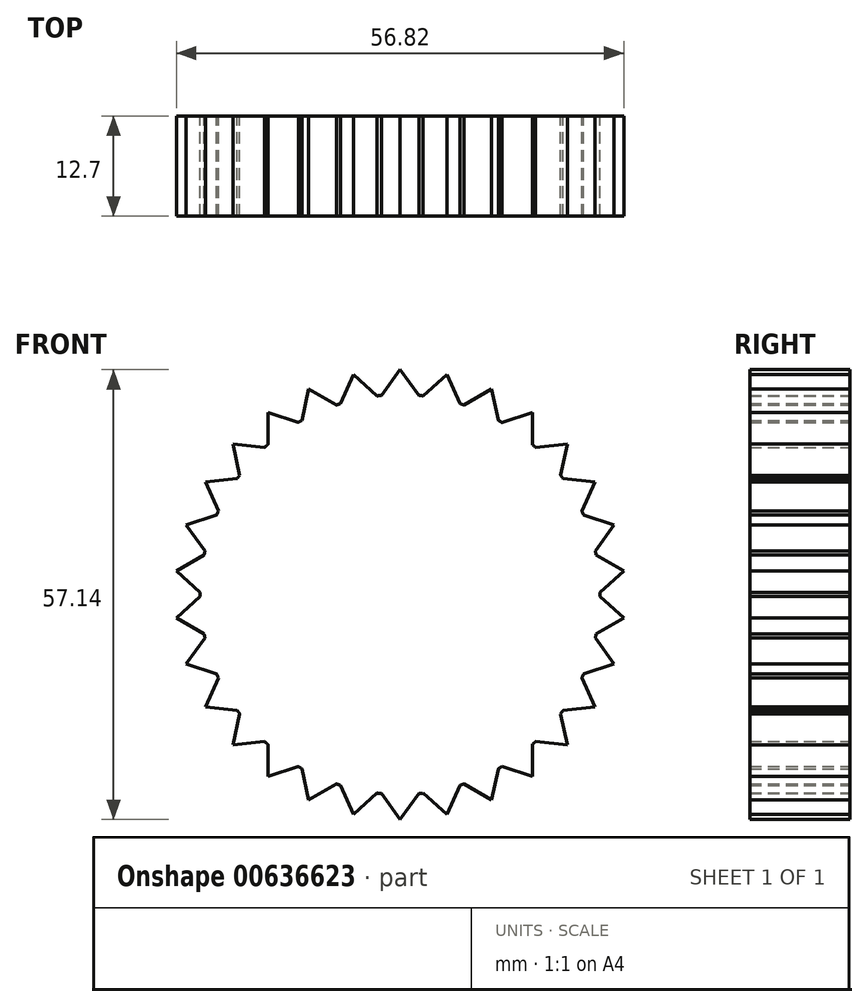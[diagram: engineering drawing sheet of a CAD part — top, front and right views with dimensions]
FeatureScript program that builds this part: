
annotation { "Feature Type Name" : "Feature", "Feature Type Description" : "" }
export const myFeature = defineFeature(function(context is Context, id is Id, definition is map)
    precondition{}
    {
        {
            var Q0;
            Q0=qCreatedBy(makeId("Front.planeOp"),FACE);
            var sketch = newSketch(context, id + "F0", { "sketchPlane" : qUnion([Q0])});
            skCircle(sketch, "E0", {"center": v(0, 0) * mm, "radius": 25.4 * mm});
            skLineSegment(sketch, "E1", {"start": v(0, 25.4) * mm, "end": v(0, 28.57) * mm, "construction": true});
            skLineSegment(sketch, "E2", {"start": v(0, 28.57) * mm, "end": v(2.38, 25.29) * mm});
            skLineSegment(sketch, "E3.MirrorCS", {"start": v(0, 28.57) * mm, "end": v(-2.38, 25.29) * mm});
            skLineSegment(sketch, "E4.1.0", {"start": v(-5.94, 27.94) * mm, "end": v(-7.59, 24.24) * mm});
            skLineSegment(sketch, "E4.1.1", {"start": v(-5.94, 27.94) * mm, "end": v(-2.93, 25.23) * mm});
            skLineSegment(sketch, "E4.2.0", {"start": v(-11.62, 26.1) * mm, "end": v(-12.46, 22.13) * mm});
            skLineSegment(sketch, "E4.2.1", {"start": v(-11.62, 26.1) * mm, "end": v(-8.1, 24.07) * mm});
            skLineSegment(sketch, "E5.2.3.0", {"start": v(-16.8, 23.11) * mm, "end": v(-16.8, 19.06) * mm});
            skLineSegment(sketch, "E5.3.3.0", {"start": v(-16.8, 23.11) * mm, "end": v(-12.94, 21.86) * mm});
            skLineSegment(sketch, "E5.2.4.0", {"start": v(-21.23, 19.12) * mm, "end": v(-20.39, 15.15) * mm});
            skLineSegment(sketch, "E5.3.4.0", {"start": v(-21.23, 19.12) * mm, "end": v(-17.2, 18.7) * mm});
            skLineSegment(sketch, "E5.2.5.0", {"start": v(-24.74, 14.28) * mm, "end": v(-23.1, 10.58) * mm});
            skLineSegment(sketch, "E5.3.5.0", {"start": v(-24.74, 14.28) * mm, "end": v(-20.7, 14.7) * mm});
            skLineSegment(sketch, "E5.2.6.0", {"start": v(-27.17, 8.83) * mm, "end": v(-24.79, 5.55) * mm});
            skLineSegment(sketch, "E5.3.6.0", {"start": v(-27.17, 8.83) * mm, "end": v(-23.31, 10.08) * mm});
            skLineSegment(sketch, "E5.2.7.0", {"start": v(-28.41, 2.99) * mm, "end": v(-25.4, 0.27) * mm});
            skLineSegment(sketch, "E5.3.7.0", {"start": v(-28.41, 2.99) * mm, "end": v(-24.9, 5.01) * mm});
            skLineSegment(sketch, "E5.2.8.0", {"start": v(-28.41, -2.99) * mm, "end": v(-24.9, -5.01) * mm});
            skLineSegment(sketch, "E5.3.8.0", {"start": v(-28.41, -2.99) * mm, "end": v(-25.4, -0.27) * mm});
            skLineSegment(sketch, "E5.2.9.0", {"start": v(-27.17, -8.83) * mm, "end": v(-23.31, -10.08) * mm});
            skLineSegment(sketch, "E5.3.9.0", {"start": v(-27.17, -8.83) * mm, "end": v(-24.79, -5.55) * mm});
            skLineSegment(sketch, "E5.2.10.0", {"start": v(-24.74, -14.28) * mm, "end": v(-20.7, -14.7) * mm});
            skLineSegment(sketch, "E5.3.10.0", {"start": v(-24.74, -14.28) * mm, "end": v(-23.1, -10.58) * mm});
            skLineSegment(sketch, "E5.2.11.0", {"start": v(-21.23, -19.12) * mm, "end": v(-17.2, -18.7) * mm});
            skLineSegment(sketch, "E5.3.11.0", {"start": v(-21.23, -19.12) * mm, "end": v(-20.39, -15.15) * mm});
            skLineSegment(sketch, "E5.2.12.0", {"start": v(-16.8, -23.11) * mm, "end": v(-12.94, -21.86) * mm});
            skLineSegment(sketch, "E5.3.12.0", {"start": v(-16.8, -23.11) * mm, "end": v(-16.8, -19.06) * mm});
            skLineSegment(sketch, "E5.2.13.0", {"start": v(-11.62, -26.1) * mm, "end": v(-8.1, -24.07) * mm});
            skLineSegment(sketch, "E5.3.13.0", {"start": v(-11.62, -26.1) * mm, "end": v(-12.46, -22.13) * mm});
            skLineSegment(sketch, "E5.2.14.0", {"start": v(-5.94, -27.94) * mm, "end": v(-2.93, -25.23) * mm});
            skLineSegment(sketch, "E5.3.14.0", {"start": v(-5.94, -27.94) * mm, "end": v(-7.59, -24.24) * mm});
            skLineSegment(sketch, "E5.2.15.0", {"start": v(0, -28.57) * mm, "end": v(2.38, -25.29) * mm});
            skLineSegment(sketch, "E5.3.15.0", {"start": v(0, -28.57) * mm, "end": v(-2.38, -25.29) * mm});
            skLineSegment(sketch, "E5.2.16.0", {"start": v(5.94, -27.94) * mm, "end": v(7.59, -24.24) * mm});
            skLineSegment(sketch, "E5.3.16.0", {"start": v(5.94, -27.94) * mm, "end": v(2.93, -25.23) * mm});
            skLineSegment(sketch, "E5.2.17.0", {"start": v(11.62, -26.1) * mm, "end": v(12.46, -22.13) * mm});
            skLineSegment(sketch, "E5.3.17.0", {"start": v(11.62, -26.1) * mm, "end": v(8.1, -24.07) * mm});
            skLineSegment(sketch, "E5.2.18.0", {"start": v(16.8, -23.11) * mm, "end": v(16.8, -19.06) * mm});
            skLineSegment(sketch, "E5.3.18.0", {"start": v(16.8, -23.11) * mm, "end": v(12.94, -21.86) * mm});
            skLineSegment(sketch, "E5.2.19.0", {"start": v(21.23, -19.12) * mm, "end": v(20.39, -15.15) * mm});
            skLineSegment(sketch, "E5.3.19.0", {"start": v(21.23, -19.12) * mm, "end": v(17.2, -18.7) * mm});
            skLineSegment(sketch, "E5.2.20.0", {"start": v(24.74, -14.28) * mm, "end": v(23.1, -10.58) * mm});
            skLineSegment(sketch, "E5.3.20.0", {"start": v(24.74, -14.28) * mm, "end": v(20.7, -14.7) * mm});
            skLineSegment(sketch, "E5.2.21.0", {"start": v(27.17, -8.83) * mm, "end": v(24.79, -5.55) * mm});
            skLineSegment(sketch, "E5.3.21.0", {"start": v(27.17, -8.83) * mm, "end": v(23.31, -10.08) * mm});
            skLineSegment(sketch, "E5.2.22.0", {"start": v(28.41, -2.99) * mm, "end": v(25.4, -0.27) * mm});
            skLineSegment(sketch, "E5.3.22.0", {"start": v(28.41, -2.99) * mm, "end": v(24.9, -5.01) * mm});
            skLineSegment(sketch, "E5.2.23.0", {"start": v(28.41, 2.99) * mm, "end": v(24.9, 5.01) * mm});
            skLineSegment(sketch, "E5.3.23.0", {"start": v(28.41, 2.99) * mm, "end": v(25.4, 0.27) * mm});
            skLineSegment(sketch, "E5.2.24.0", {"start": v(27.17, 8.83) * mm, "end": v(23.31, 10.08) * mm});
            skLineSegment(sketch, "E5.3.24.0", {"start": v(27.17, 8.83) * mm, "end": v(24.79, 5.55) * mm});
            skLineSegment(sketch, "E5.2.25.0", {"start": v(24.74, 14.28) * mm, "end": v(20.7, 14.7) * mm});
            skLineSegment(sketch, "E5.3.25.0", {"start": v(24.74, 14.28) * mm, "end": v(23.1, 10.58) * mm});
            skLineSegment(sketch, "E5.2.26.0", {"start": v(21.23, 19.12) * mm, "end": v(17.2, 18.7) * mm});
            skLineSegment(sketch, "E5.3.26.0", {"start": v(21.23, 19.12) * mm, "end": v(20.39, 15.15) * mm});
            skLineSegment(sketch, "E5.2.27.0", {"start": v(16.8, 23.11) * mm, "end": v(12.94, 21.86) * mm});
            skLineSegment(sketch, "E5.3.27.0", {"start": v(16.8, 23.11) * mm, "end": v(16.8, 19.06) * mm});
            skLineSegment(sketch, "E5.2.28.0", {"start": v(11.62, 26.1) * mm, "end": v(8.1, 24.07) * mm});
            skLineSegment(sketch, "E5.3.28.0", {"start": v(11.62, 26.1) * mm, "end": v(12.46, 22.13) * mm});
            skLineSegment(sketch, "E5.2.29.0", {"start": v(5.94, 27.94) * mm, "end": v(2.93, 25.23) * mm});
            skLineSegment(sketch, "E5.3.29.0", {"start": v(5.94, 27.94) * mm, "end": v(7.59, 24.24) * mm});
            skSolve(sketch);
        }
        {
            var Q0;
            Q0 = qSketchRegion(id + "F0", true);
            extrude(context, id + "F1", {"entities" : qUnion([Q0]), "depth" : 12.7 * mm, "offsetDistance" : 25.4 * mm});
        }
    });
